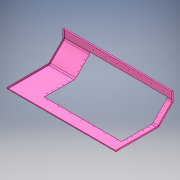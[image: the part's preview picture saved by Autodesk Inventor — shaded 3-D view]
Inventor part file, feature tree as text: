
AUTODESK INVENTOR PART (.ipt)
format: ipt  version: 2018 (Build 220112000, 112)  size: 347,648 bytes
history: native  units: mm
features: sheet_metal_op x13, sketch x10, other x5, hole x4, extrude x1
ambient origin geometry x8: Origin, YZ Plane, XZ Plane, XY Plane, X Axis, Y Axis, Z Axis, Center Point
bodies: Solid1 (feature_tree)
feature tree (33):
  sheet_metal_op  "Face1"
  sheet_metal_op  "Flange1"
  sheet_metal_op  "Flange2"
  extrude  "Extrusion1"  Depth=550.0mm
  sheet_metal_op  "Flange3"
  sheet_metal_op  "Flange4"
  sketch  "Sketch12"  dims[d13=1.6mm]
  sketch  "Sketch13"  dims[d14=0.8mm]
  sketch  "Sketch14"  dims[d15=3.2mm]
  hole  "Hole1"  [1 undecoded]
  hole  "Hole2"  [1 undecoded]
  hole  "Hole3"  [1 undecoded]
  hole  "Hole4"  [1 undecoded]
  sketch  "Sketch1"  dims[d0=1410.0mm d1=550.0mm]
  other  "Plate1"
  sketch  "Sketch2"  dims[d2=1.6mm d3=1.6mm]
  other  "Plate2"
  sheet_metal_op  "Bend1"
  sheet_metal_op  "Corner1"
  sketch  "Sketch3"  dims[d4=0.8mm d5=3.2mm]
  other  "Plate3"
  sheet_metal_op  "Bend2"
  sheet_metal_op  "Corner2"
  sketch  "Sketch4"  dims[d6=1.6mm d7=270.0mm d8=45.0deg d9=30.0mm]
  sketch  "Sketch5"  dims[d10=6.4mm d11=1.6mm]
  other  "Plate4"
  sheet_metal_op  "Bend3"
  sheet_metal_op  "Corner3"
  sketch  "Sketch6"  dims[d12=1.6mm]
  other  "Plate5"
  sheet_metal_op  "Bend4"
  sheet_metal_op  "Corner4"
  sketch  "Sketch15"  dims[d16=1.6mm d17=125.0mm d18=45.0deg d19=30.0mm d20=6.4mm d21=1.6mm d22=1.6mm d23=1000.0mm d24=1000.0mm d25=150.0mm d26=210.0mm d27=0.0mm d28=1.6mm d29=0.8mm d30=3.2mm d31=1.6mm d32=20.0mm d33=90.0deg d34=1.6mm d35=6.4mm d36=1.6mm d37=1.6mm d38=1.6mm d39=0.8mm d40=3.2mm d41=1.6mm d42=20.0mm d43=12.217305mm d44=1.6mm d45=6.4mm d46=1.6mm d47=1.6mm d48=80.0mm d88=15.0mm d89=500.0mm d90=40.0mm d92=150.0mm d93=10.0mm d95=10.0mm d97=40.0mm d99=150.0mm d100=10.0mm d102=10.0mm d104=45.0mm d105=500.0mm d106=40.0mm d108=150.0mm d109=40.0mm d111=150.0mm d114=20.0mm d115=193.5mm d116=30.0mm d118=70.0mm d119=30.0mm d121=70.0mm d124=20.0mm d125=193.5mm d126=30.0mm d128=70.0mm d129=30.0mm d131=70.0mm d134=20.0mm d135=122.0mm d136=20.0mm d138=60.0mm d139=20.0mm d141=60.0mm d144=20.0mm d145=122.0mm d146=20.0mm d148=60.0mm d149=20.0mm d151=60.0mm d154=5.0mm d155=6.0mm d156=7.0mm d157=2.0mm d158=90.0deg d159=1.6mm d160=20.594885mm d161=5.0mm d162=6.0mm d163=7.0mm d164=2.0mm d165=90.0deg d166=1.6mm d167=20.594885mm d168=5.0mm d169=6.0mm d170=7.0mm d171=2.0mm d172=90.0deg d173=1.6mm d174=20.594885mm d175=5.0mm d176=6.0mm d177=7.0mm d178=2.0mm d179=90.0deg d180=1.6mm d181=20.594885mm]
note: 4 required parameter values undecoded (feature->parameter linkage not recoverable at this tier; creation-order binding heuristic only, values carry confidence <= 0.55)
